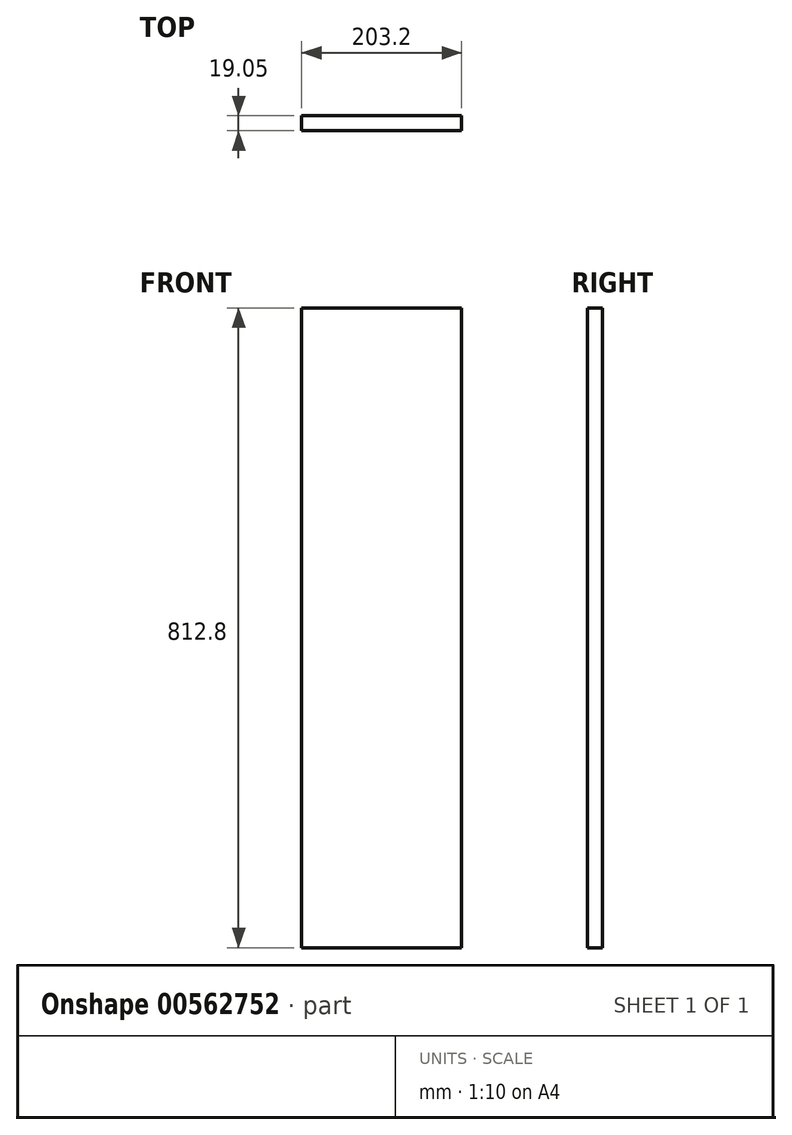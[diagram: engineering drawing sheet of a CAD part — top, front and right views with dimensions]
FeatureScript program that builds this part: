
annotation { "Feature Type Name" : "Feature", "Feature Type Description" : "" }
export const myFeature = defineFeature(function(context is Context, id is Id, definition is map)
    precondition{}
    {
        {
            var Q0;
            Q0=qCreatedBy(makeId("Front.planeOp"),FACE);
            var sketch = newSketch(context, id + "F0", { "sketchPlane" : qUnion([Q0])});
            skLineSegment(sketch, "E0.bottom", {"start": v(-101.6, -406.4) * mm, "end": v(101.6, -406.4) * mm});
            skLineSegment(sketch, "E0.top", {"start": v(-101.6, 406.4) * mm, "end": v(101.6, 406.4) * mm});
            skLineSegment(sketch, "E0.left", {"start": v(-101.6, -406.4) * mm, "end": v(-101.6, 406.4) * mm});
            skLineSegment(sketch, "E0.right", {"start": v(101.6, -406.4) * mm, "end": v(101.6, 406.4) * mm});
            skPoint(sketch, "E0.middle", {"position": v(0, 0) * mm});
            skSolve(sketch);
        }
        {
            var Q0;
            Q0 = qSketchRegion(id + "F0", true);
            extrude(context, id + "F1", {"entities" : qUnion([Q0]), "depth" : 19.05 * mm, "offsetDistance" : 25.4 * mm});
        }
    });
